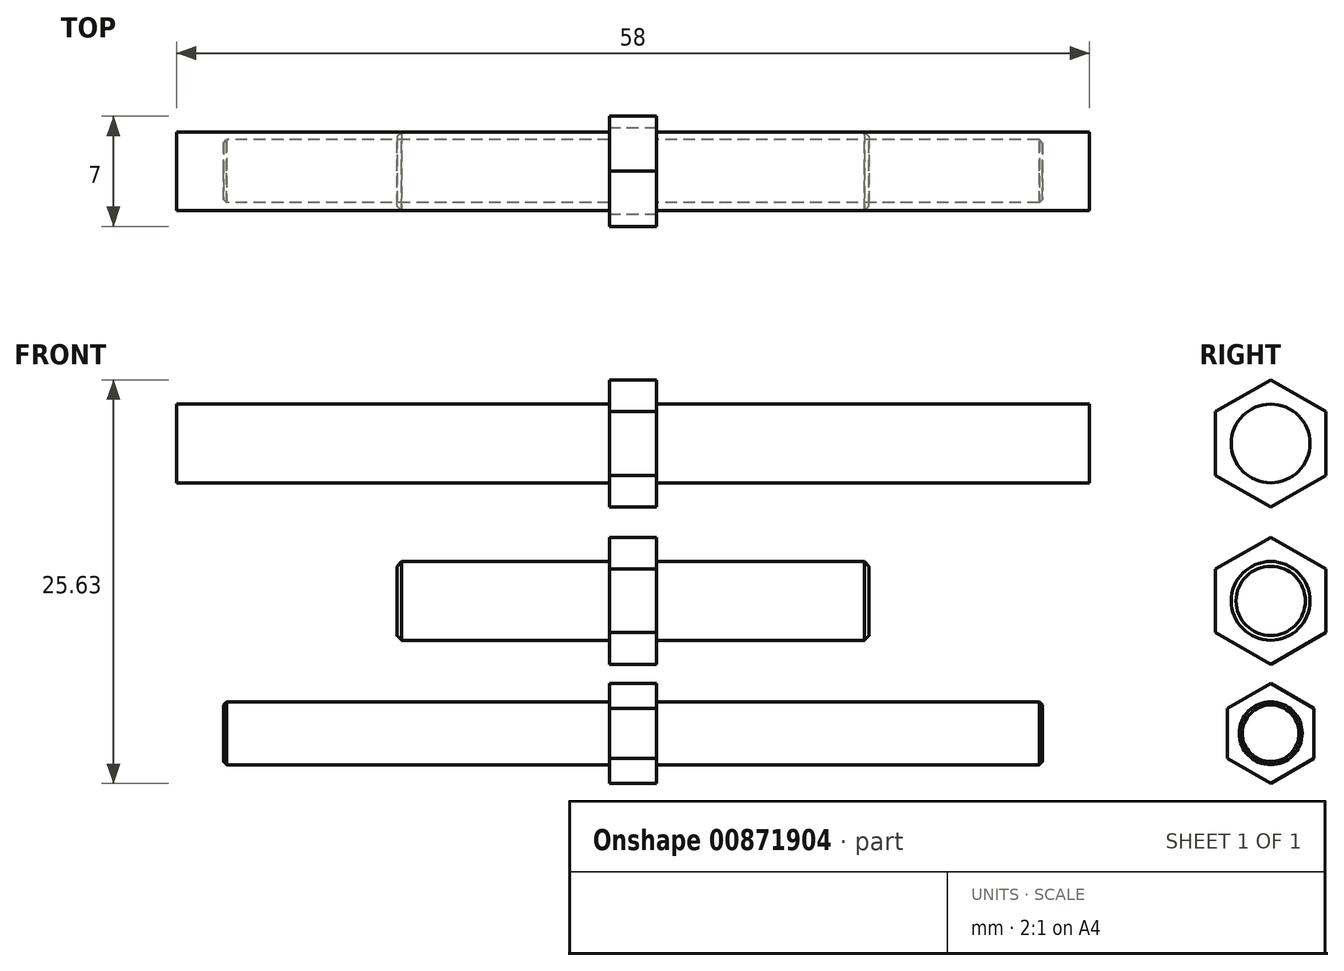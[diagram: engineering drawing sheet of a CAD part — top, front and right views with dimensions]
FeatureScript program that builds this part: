
annotation { "Feature Type Name" : "Feature", "Feature Type Description" : "" }
export const myFeature = defineFeature(function(context is Context, id is Id, definition is map)
    precondition{}
    {
        {
            var Q0;
            Q0=qCreatedBy(makeId("Right.planeOp"),FACE);
            var sketch = newSketch(context, id + "F0", { "sketchPlane" : qUnion([Q0])});
            skCircle(sketch, "E0", {"center": v(0, 0) * mm, "radius": 2 * mm});
            skSolve(sketch);
        }
        {
            var Q0;
            Q0=qSketchRegion(id+"F0",true);
            extrude(context, id + "F1", {"entities" : qUnion([Q0]), "depth" : 52 * mm, "offsetDistance" : 25 * mm, "symmetric" : true});
        }
        {
            var Q0;
            Q0=qCreatedBy(makeId("Right.planeOp"),FACE);
            var sketch = newSketch(context, id + "F2", { "sketchPlane" : qUnion([Q0])});
            skCircle(sketch, "E1.cCircle", {"center": v(0, 0) * mm, "radius": 2.75 * mm, "construction": true});
            skLineSegment(sketch, "E1.0", {"start": v(2.75, 1.59) * mm, "end": v(2.75, -1.59) * mm});
            skLineSegment(sketch, "E1.1", {"start": v(2.75, -1.59) * mm, "end": v(0, -3.18) * mm});
            skLineSegment(sketch, "E1.2", {"start": v(0, -3.18) * mm, "end": v(-2.75, -1.59) * mm});
            skLineSegment(sketch, "E1.3", {"start": v(-2.75, -1.59) * mm, "end": v(-2.75, 1.59) * mm});
            skLineSegment(sketch, "E1.4", {"start": v(-2.75, 1.59) * mm, "end": v(0, 3.18) * mm});
            skLineSegment(sketch, "E1.5", {"start": v(0, 3.18) * mm, "end": v(2.75, 1.59) * mm});
            skPoint(sketch, "E1.0.midPoint", {"position": v(2.75, 0) * mm});
            skLineSegment(sketch, "E2", {"start": v(0, 0) * mm, "end": v(0, -4.6) * mm, "construction": true});
            skSolve(sketch);
        }
        {
            var Q0;
            Q0=makeQuery(id+"F2.imprint","IMPRINT",FACE,{"disambiguationData":[TD([[makeQuery(id+"F2.imprint","IMPRINT",EDGE,{"derivedFrom":sQuery(id+"F2.wireOp",EDGE,"E1.0")}),-1.0]])]});
            extrude(context, id + "F3", {"entities" : qUnion([Q0]), "operationType" : NewBodyOperationType.ADD, "depth" : 3 * mm, "offsetDistance" : 25 * mm, "symmetric" : true});
        }
        {
            var Q0;
            Q0=qCreatedBy(makeId("Right.planeOp"),FACE);
            var sketch = newSketch(context, id + "F4", { "sketchPlane" : qUnion([Q0])});
            skCircle(sketch, "E3", {"center": v(0, 8.41) * mm, "radius": 2.5 * mm});
            skSolve(sketch);
        }
        {
            var Q0;
            Q0=makeQuery(id+"F4.imprint","IMPRINT",FACE,{"disambiguationData":[TD([[makeQuery(id+"F4.imprint","IMPRINT",EDGE,{"derivedFrom":sQuery(id+"F4.wireOp",EDGE,"E3")}),1.0]])]});
            extrude(context, id + "F5", {"entities" : qUnion([Q0]), "depth" : 30 * mm, "offsetDistance" : 25 * mm, "symmetric" : true});
        }
        {
            var Q0;
            Q0=qCreatedBy(makeId("Right.planeOp"),FACE);
            var sketch = newSketch(context, id + "F6", { "sketchPlane" : qUnion([Q0])});
            skCircle(sketch, "E4.0", {"center": v(0, 8.41) * mm, "radius": 2.5 * mm, "construction": true});
            skLineSegment(sketch, "E5", {"start": v(0, 8.41) * mm, "end": v(0, 14.45) * mm, "construction": true});
            skCircle(sketch, "E6.cCircle", {"center": v(0, 8.41) * mm, "radius": 3.5 * mm, "construction": true});
            skLineSegment(sketch, "E6.0", {"start": v(0, 12.45) * mm, "end": v(3.5, 10.43) * mm});
            skLineSegment(sketch, "E6.1", {"start": v(3.5, 10.43) * mm, "end": v(3.5, 6.4) * mm});
            skLineSegment(sketch, "E6.2", {"start": v(3.5, 6.4) * mm, "end": v(0, 4.37) * mm});
            skLineSegment(sketch, "E6.3", {"start": v(0, 4.37) * mm, "end": v(-3.5, 6.4) * mm});
            skLineSegment(sketch, "E6.4", {"start": v(-3.5, 6.4) * mm, "end": v(-3.5, 10.43) * mm});
            skLineSegment(sketch, "E6.5", {"start": v(-3.5, 10.43) * mm, "end": v(0, 12.45) * mm});
            skPoint(sketch, "E6.0.midPoint", {"position": v(1.75, 11.44) * mm});
            skSolve(sketch);
        }
        {
            var Q0;
            Q0=makeQuery(id+"F6.imprint","IMPRINT",FACE,{"disambiguationData":[TD([[makeQuery(id+"F6.imprint","IMPRINT",EDGE,{"derivedFrom":sQuery(id+"F6.wireOp",EDGE,"E6.0")}),-1.0]])]});
            extrude(context, id + "F7", {"entities" : qUnion([Q0]), "operationType" : NewBodyOperationType.ADD, "depth" : 3 * mm, "offsetDistance" : 25 * mm, "symmetric" : true});
        }
        {
            var Q0;
            Q0=makeQuery(id+"F1.opExtrude","CAP_EDGE",EDGE,{"disambiguationData":[OSD([sQuery(id+"F0.wireOp",EDGE,"E0")])],"isStart":false});
            var Q1;
            Q1=makeQuery(id+"F1.opExtrude","CAP_EDGE",EDGE,{"disambiguationData":[OSD([sQuery(id+"F0.wireOp",EDGE,"E0")])],"isStart":true});
            chamfer(context, id + "F8", {"entities" : qUnion([Q0, Q1]), "width" : 0.2 * mm, "tangentPropagation" : true});
        }
        {
            var Q0;
            Q0=makeQuery(id+"F5.opExtrude","SWEPT_BODY",BODY,{"disambiguationData":[OSD([sQuery(id+"F4.wireOp",EDGE,"E3")])]});
            transform(context, id + "F9", {"entities" : qUnion([Q0]), "transformType" : TransformType.TRANSLATION_3D, "dx" : 0 * mm, "dy" : 0 * mm, "dz" : 10 * mm, "makeCopy" : true});
        }
        {
            var Q0;
            Q0=makeQuery(id+"F5.opExtrude","CAP_EDGE",EDGE,{"disambiguationData":[OSD([sQuery(id+"F4.wireOp",EDGE,"E3")])],"isStart":true});
            var Q1;
            Q1=makeQuery(id+"F5.opExtrude","CAP_EDGE",EDGE,{"disambiguationData":[OSD([sQuery(id+"F4.wireOp",EDGE,"E3")])],"isStart":false});
            chamfer(context, id + "F10", {"entities" : qUnion([Q0, Q1]), "width" : 0.3 * mm, "tangentPropagation" : true});
        }
        {
            var Q0;
            Q0=makeQuery(id+"F9.opPattern","COPY",FACE,{"derivedFrom":makeQuery(id+"F5.opExtrude","CAP_FACE",FACE,{"disambiguationData":[OSD([sQuery(id+"F4.wireOp",EDGE,"E3")])],"isStart":true}),"instanceName":"1"});
            extrude(context, id + "F11", {"entities" : qUnion([Q0]), "operationType" : NewBodyOperationType.ADD, "depth" : ((58 - 30) / 2) * mm, "offsetDistance" : 25 * mm});
        }
        {
            var Q0;
            Q0=makeQuery(id+"F9.opPattern","COPY",FACE,{"derivedFrom":makeQuery(id+"F5.opExtrude","CAP_FACE",FACE,{"disambiguationData":[OSD([sQuery(id+"F4.wireOp",EDGE,"E3")])],"isStart":false}),"instanceName":"1"});
            extrude(context, id + "F12", {"entities" : qUnion([Q0]), "operationType" : NewBodyOperationType.ADD, "depth" : 14 * mm, "offsetDistance" : 25 * mm});
        }
    });
